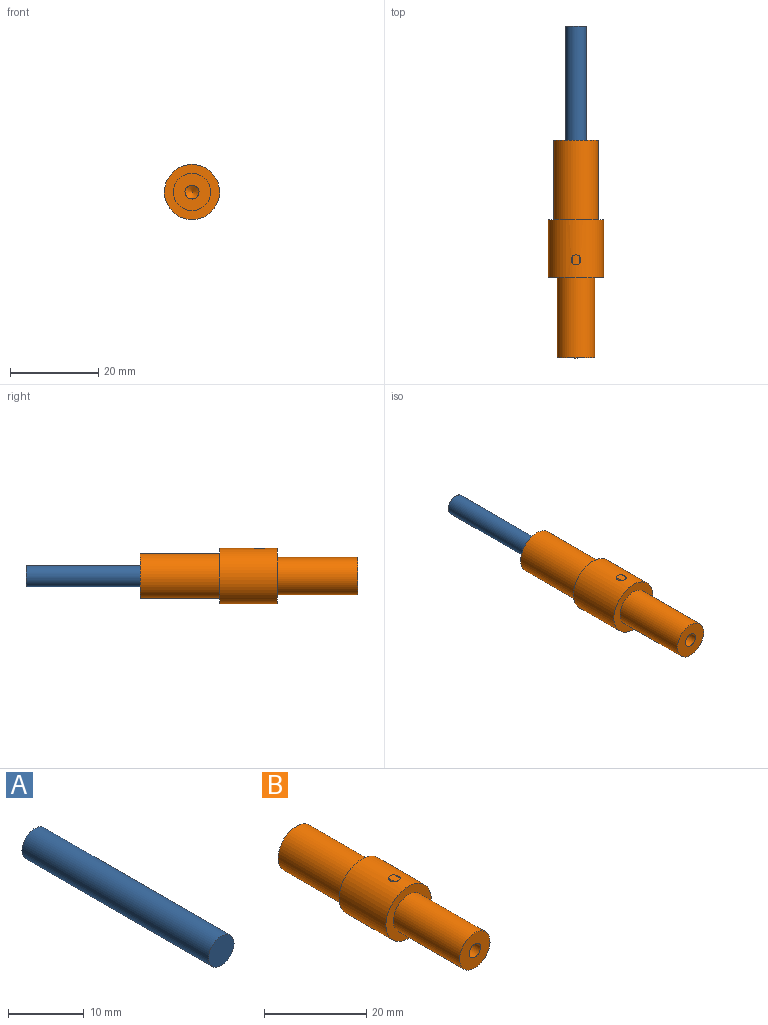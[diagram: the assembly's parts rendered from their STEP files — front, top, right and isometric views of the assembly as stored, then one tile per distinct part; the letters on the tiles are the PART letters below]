
ASSEMBLY  parts=2 mates=1
PART A: 3 faces, bbox 4.8x34.9x4.8 mm
  f0: cylinder r=2.38mm len=34.93mm, axis (0,1,0), area 522.5mm2, adj f1,f2
  f1: plane 4.76x4.76mm, normal (0,-1,0), area 17.8mm2, adj f0
  f2: plane 4.76x4.76mm, normal (0,1,0), area 17.8mm2, adj f0
PART B: 13 faces, bbox 12.5x49.3x12.5 mm
  f0: cylinder r=6.25mm len=12.95mm, axis (0,1,0), area 507.8mm2, adj f5,f6,f11,f12
  f1: cylinder r=1.59mm len=25.4mm, axis (0,-1,0), area 249mm2, adj f2,f8,f12
  f2: plane 8.43x8.43mm, normal (0,-1,0), area 47.9mm2, adj f1,f7
  f3: plane 10.16x10.16mm, normal (0,1,0), area 63.4mm2, adj f4,f10
  f4: cylinder r=5.08mm len=18.06mm, axis (0,1,0), area 576.4mm2, adj f3,f5
  f5: plane 12.5x12.5mm, normal (0,1,0), area 41.6mm2, adj f0,f4
  f6: plane 12.5x12.5mm, normal (0,-1,0), area 66.8mm2, adj f0,f7
  f7: cylinder r=4.22mm len=18.31mm, axis (0,1,0), area 485.2mm2, adj f2,f6
  f8: cone r=0mm half-angle=59deg, axis (0,-1,0), area 9.2mm2, adj f1
  f9: cone r=0mm half-angle=59deg, axis (0,1,0), area 20.7mm2, adj f10
  f10: cylinder r=2.37mm len=9.53mm, axis (0,1,0), area 142.1mm2, adj f3,f9
  f11: plane 2.26x1.59mm, normal (0,0,-1), area 3.3mm2, adj f0,f12
  f12: cylinder r=1.13mm len=5.08mm, axis (0,0,1), area 34.2mm2, adj f0,f1,f11
PLACE A t=(12.2,75.22,12.14)mm
PLACE B at identity
MATE fastened A.f0 <-> B.f0  axis (0,-1,0) through (0,40.3,0)mm
